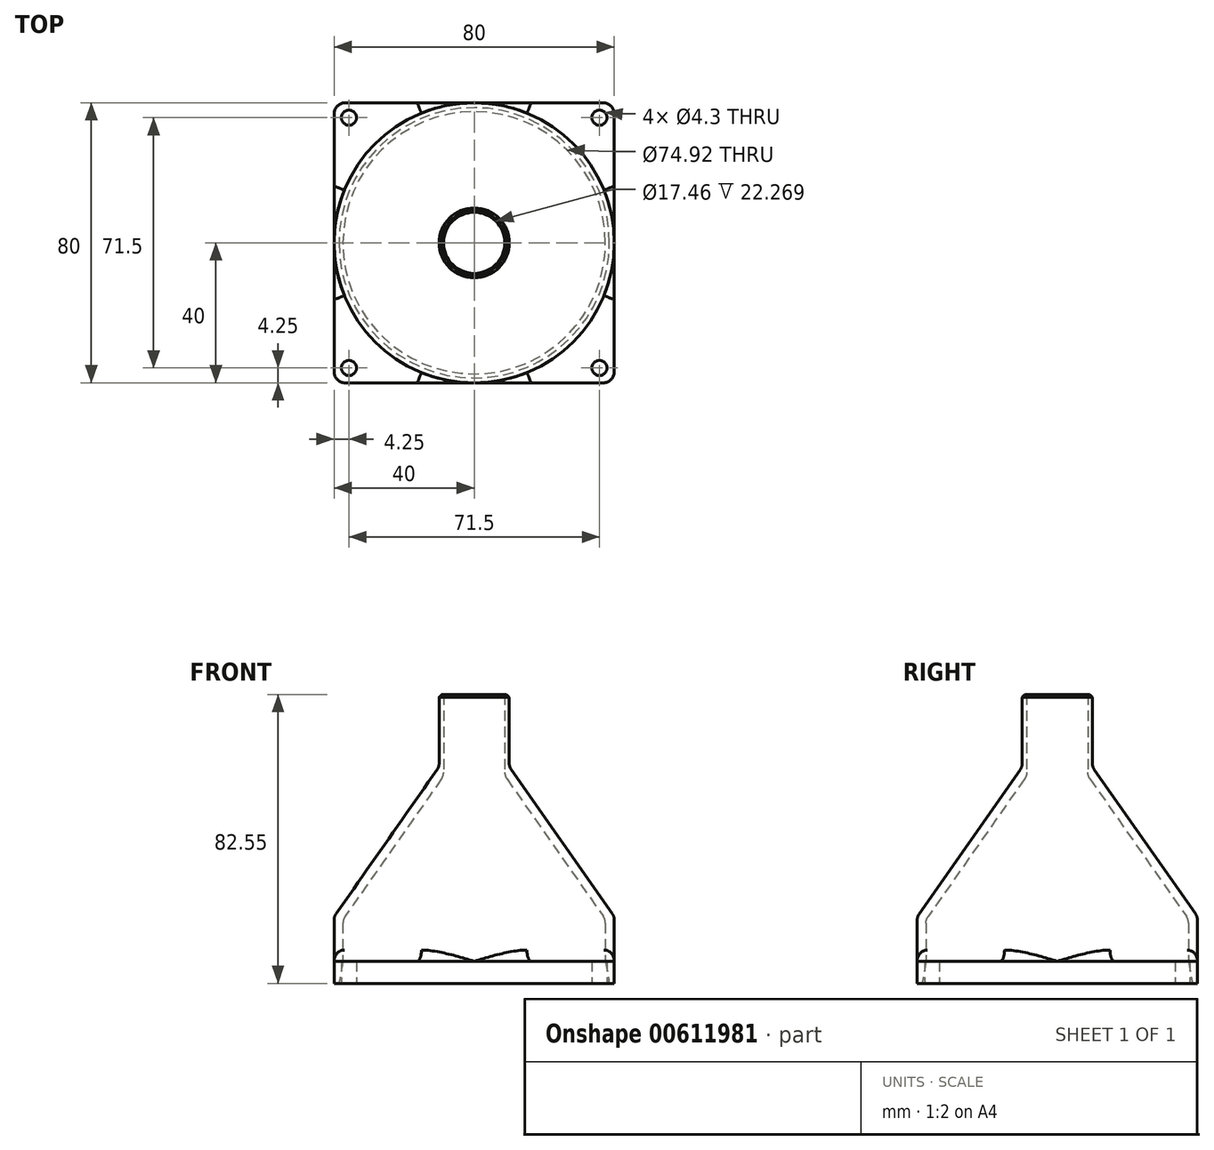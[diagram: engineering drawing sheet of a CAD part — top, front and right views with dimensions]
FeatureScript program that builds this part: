
annotation { "Feature Type Name" : "Feature", "Feature Type Description" : "" }
export const myFeature = defineFeature(function(context is Context, id is Id, definition is map)
    precondition{}
    {
        {
            var Q0;
            Q0=qCreatedBy(makeId("Top.planeOp"),FACE);
            var sketch = newSketch(context, id + "F0", { "sketchPlane" : qUnion([Q0])});
            skLineSegment(sketch, "E0.bottom", {"start": v(40, 40) * mm, "end": v(-40, 40) * mm});
            skLineSegment(sketch, "E0.top", {"start": v(40, -40) * mm, "end": v(-40, -40) * mm});
            skLineSegment(sketch, "E0.left", {"start": v(40, 40) * mm, "end": v(40, -40) * mm});
            skLineSegment(sketch, "E0.right", {"start": v(-40, 40) * mm, "end": v(-40, -40) * mm});
            skPoint(sketch, "E0.middle", {"position": v(0, 0) * mm});
            skSolve(sketch);
        }
        {
            var Q0;
            Q0 = qSketchRegion(id + "F0", true);
            extrude(context, id + "F1", {"entities" : qUnion([Q0]), "oppositeDirection" : true, "depth" : 6.35 * mm, "offsetDistance" : 25.4 * mm});
        }
        {
            var Q0;
            Q0=qCreatedBy(makeId("Front.planeOp"),FACE);
            var sketch = newSketch(context, id + "F2", { "sketchPlane" : qUnion([Q0])});
            skLineSegment(sketch, "E1", {"start": v(0, 0) * mm, "end": v(0, -6.35) * mm});
            skLineSegment(sketch, "E2", {"start": v(38.6, -6.35) * mm, "end": v(37.46, 0) * mm});
            skLineSegment(sketch, "E3", {"start": v(37.46, 0) * mm, "end": v(0, 0) * mm});
            skLineSegment(sketch, "E4", {"start": v(0, -6.35) * mm, "end": v(38.6, -6.35) * mm});
            skLineSegment(sketch, "E5", {"start": v(0, 0) * mm, "end": v(0, 10.75) * mm, "construction": true});
            skSolve(sketch);
        }
        {
            var Q0;
            Q0 = qSketchRegion(id + "F2", true);
            var Q1;
            Q1=sQuery(id+"F2.wireOp",EDGE,"E5");
            revolve(context, id + "F3", {"operationType" : NewBodyOperationType.REMOVE, "entities" : qUnion([Q0]), "axis" : qUnion([Q1]), "revolveType" : RevolveType.FULL, "oppositeDirection" : true});
        }
        {
            var Q0;
            Q0=qCreatedBy(makeId("Front.planeOp"),FACE);
            var sketch = newSketch(context, id + "F4", { "sketchPlane" : qUnion([Q0])});
            skLineSegment(sketch, "E6", {"start": v(37.46, 0) * mm, "end": v(37.46, 11.9) * mm});
            skLineSegment(sketch, "E7", {"start": v(37.46, 11.9) * mm, "end": v(8.73, 52.93) * mm});
            skLineSegment(sketch, "E8", {"start": v(8.73, 52.93) * mm, "end": v(8.73, 76.2) * mm});
            skLineSegment(sketch, "E9", {"start": v(8.73, 76.2) * mm, "end": v(10, 76.2) * mm});
            skLineSegment(sketch, "E10", {"start": v(10, 76.2) * mm, "end": v(10, 55.54) * mm});
            skLineSegment(sketch, "E11", {"start": v(10, 55.54) * mm, "end": v(40, 12.7) * mm});
            skLineSegment(sketch, "E12", {"start": v(40, 12.7) * mm, "end": v(40, 0) * mm});
            skLineSegment(sketch, "E13", {"start": v(40, 0) * mm, "end": v(37.46, 0) * mm});
            skLineSegment(sketch, "E14.0", {"start": v(-37.46, 0) * mm, "end": v(37.46, 0) * mm, "construction": true});
            skLineSegment(sketch, "E15", {"start": v(0, 0) * mm, "end": v(0, 76.2) * mm, "construction": true});
            skSolve(sketch);
        }
        {
            var Q0;
            Q0=makeQuery(id+"F4.imprint","IMPRINT",FACE,{"disambiguationData":[TD([[makeQuery(id+"F4.imprint","IMPRINT",EDGE,{"derivedFrom":sQuery(id+"F4.wireOp",EDGE,"E6")}),-1.0]])]});
            var Q1;
            Q1=sQuery(id+"F4.wireOp",EDGE,"E15");
            revolve(context, id + "F5", {"operationType" : NewBodyOperationType.ADD, "entities" : qUnion([Q0]), "axis" : qUnion([Q1]), "revolveType" : RevolveType.FULL});
        }
        {
            var Q0;
            Q0=makeQuery(id+"F1.opExtrude","CAP_FACE",FACE,{"disambiguationData":[OSD([sQuery(id+"F0.wireOp",EDGE,"E0.bottom"),sQuery(id+"F0.wireOp",EDGE,"E0.top"),sQuery(id+"F0.wireOp",EDGE,"E0.left"),sQuery(id+"F0.wireOp",EDGE,"E0.right")])],"isStart":false});
            var sketch = newSketch(context, id + "F6", { "sketchPlane" : qUnion([Q0])});
            skCircle(sketch, "E16", {"center": v(35.75, 35.75) * mm, "radius": 2.15 * mm});
            skCircle(sketch, "E17", {"center": v(-35.75, 35.75) * mm, "radius": 2.15 * mm});
            skCircle(sketch, "E18", {"center": v(-35.75, -35.75) * mm, "radius": 2.15 * mm});
            skCircle(sketch, "E19", {"center": v(35.75, -35.75) * mm, "radius": 2.15 * mm});
            skLineSegment(sketch, "E20", {"start": v(-35.75, -35.75) * mm, "end": v(35.75, 35.75) * mm, "construction": true});
            skSolve(sketch);
        }
        {
            var Q0;
            Q0 = qSketchRegion(id + "F6", true);
            extrude(context, id + "F7", {"entities" : qUnion([Q0]), "operationType" : NewBodyOperationType.REMOVE, "endBound" : BoundingType.UP_TO_NEXT, "oppositeDirection" : true, "depth" : 25.4 * mm, "offsetDistance" : 25.4 * mm});
        }
        {
            var Q0;
            Q0=makeQuery(id+"F5.opRevolve","SWEPT_EDGE",EDGE,{"disambiguationData":[OSD([sQuery(id+"F4.wireOp",EDGE,"E9"),sQuery(id+"F4.wireOp",EDGE,"E10")])]});
            chamfer(context, id + "F8", {"entities" : qUnion([Q0]), "width" : 0.76 * mm, "tangentPropagation" : true});
        }
        {
            var Q0;
            {var subQ0=sQuery(id+"F0.wireOp",EDGE,"E0.right");var subQ1=sQuery(id+"F0.wireOp",EDGE,"E0.top");var subQ2=sQuery(id+"F4.wireOp",EDGE,"E12");Q0=makeQuery(id+"F5.boolean.opBoolean","SPLIT",EDGE,{"disambiguationData":[TD([makeQuery(id+"F1.opExtrude","CAP_FACE",FACE,{"disambiguationData":[OSD([sQuery(id+"F0.wireOp",EDGE,"E0.bottom"),subQ1,sQuery(id+"F0.wireOp",EDGE,"E0.left"),subQ0])],"isStart":true}),makeQuery(id+"F1.opExtrude","SWEPT_FACE",FACE,{"disambiguationData":[OSD([subQ1])]}),makeQuery(id+"F1.opExtrude","SWEPT_FACE",FACE,{"disambiguationData":[OSD([subQ0])]}),makeQuery(id+"F5.opRevolve","SWEPT_FACE",FACE,{"disambiguationData":[OSD([subQ2])]})])],"derivedFrom":makeQuery(id+"F5.opRevolve","SWEPT_EDGE",EDGE,{"disambiguationData":[OSD([subQ2,sQuery(id+"F4.wireOp",EDGE,"E13")])]})});}
            var Q1;
            {var subQ0=sQuery(id+"F0.wireOp",EDGE,"E0.left");var subQ1=sQuery(id+"F0.wireOp",EDGE,"E0.top");var subQ2=sQuery(id+"F4.wireOp",EDGE,"E12");Q1=makeQuery(id+"F5.boolean.opBoolean","SPLIT",EDGE,{"disambiguationData":[TD([makeQuery(id+"F1.opExtrude","CAP_FACE",FACE,{"disambiguationData":[OSD([sQuery(id+"F0.wireOp",EDGE,"E0.bottom"),subQ1,subQ0,sQuery(id+"F0.wireOp",EDGE,"E0.right")])],"isStart":true}),makeQuery(id+"F1.opExtrude","SWEPT_FACE",FACE,{"disambiguationData":[OSD([subQ1])]}),makeQuery(id+"F1.opExtrude","SWEPT_FACE",FACE,{"disambiguationData":[OSD([subQ0])]}),makeQuery(id+"F5.opRevolve","SWEPT_FACE",FACE,{"disambiguationData":[OSD([subQ2])]})])],"derivedFrom":makeQuery(id+"F5.opRevolve","SWEPT_EDGE",EDGE,{"disambiguationData":[OSD([subQ2,sQuery(id+"F4.wireOp",EDGE,"E13")])]})});}
            var Q2;
            {var subQ0=sQuery(id+"F0.wireOp",EDGE,"E0.bottom");var subQ1=sQuery(id+"F0.wireOp",EDGE,"E0.left");var subQ2=sQuery(id+"F4.wireOp",EDGE,"E12");Q2=makeQuery(id+"F5.boolean.opBoolean","SPLIT",EDGE,{"disambiguationData":[TD([makeQuery(id+"F1.opExtrude","SWEPT_FACE",FACE,{"disambiguationData":[OSD([subQ0])]}),makeQuery(id+"F1.opExtrude","CAP_FACE",FACE,{"disambiguationData":[OSD([subQ0,sQuery(id+"F0.wireOp",EDGE,"E0.top"),subQ1,sQuery(id+"F0.wireOp",EDGE,"E0.right")])],"isStart":true}),makeQuery(id+"F1.opExtrude","SWEPT_FACE",FACE,{"disambiguationData":[OSD([subQ1])]}),makeQuery(id+"F5.opRevolve","SWEPT_FACE",FACE,{"disambiguationData":[OSD([subQ2])]})])],"derivedFrom":makeQuery(id+"F5.opRevolve","SWEPT_EDGE",EDGE,{"disambiguationData":[OSD([subQ2,sQuery(id+"F4.wireOp",EDGE,"E13")])]})});}
            var Q3;
            {var subQ0=sQuery(id+"F0.wireOp",EDGE,"E0.bottom");var subQ1=sQuery(id+"F0.wireOp",EDGE,"E0.right");var subQ2=sQuery(id+"F4.wireOp",EDGE,"E12");Q3=makeQuery(id+"F5.boolean.opBoolean","SPLIT",EDGE,{"disambiguationData":[TD([makeQuery(id+"F1.opExtrude","SWEPT_FACE",FACE,{"disambiguationData":[OSD([subQ0])]}),makeQuery(id+"F1.opExtrude","CAP_FACE",FACE,{"disambiguationData":[OSD([subQ0,sQuery(id+"F0.wireOp",EDGE,"E0.top"),sQuery(id+"F0.wireOp",EDGE,"E0.left"),subQ1])],"isStart":true}),makeQuery(id+"F1.opExtrude","SWEPT_FACE",FACE,{"disambiguationData":[OSD([subQ1])]}),makeQuery(id+"F5.opRevolve","SWEPT_FACE",FACE,{"disambiguationData":[OSD([subQ2])]})])],"derivedFrom":makeQuery(id+"F5.opRevolve","SWEPT_EDGE",EDGE,{"disambiguationData":[OSD([subQ2,sQuery(id+"F4.wireOp",EDGE,"E13")])]})});}
            var Q4;
            Q4=makeQuery(id+"F5.opRevolve","SWEPT_EDGE",EDGE,{"disambiguationData":[OSD([sQuery(id+"F4.wireOp",EDGE,"E11"),sQuery(id+"F4.wireOp",EDGE,"E12")])]});
            var Q5;
            Q5=makeQuery(id+"F5.opRevolve","SWEPT_EDGE",EDGE,{"disambiguationData":[OSD([sQuery(id+"F4.wireOp",EDGE,"E6"),sQuery(id+"F4.wireOp",EDGE,"E7")])]});
            var Q6;
            Q6=makeQuery(id+"F5.opRevolve","SWEPT_EDGE",EDGE,{"disambiguationData":[OSD([sQuery(id+"F4.wireOp",EDGE,"E10"),sQuery(id+"F4.wireOp",EDGE,"E11")])]});
            var Q7;
            Q7=makeQuery(id+"F5.opRevolve","SWEPT_EDGE",EDGE,{"disambiguationData":[OSD([sQuery(id+"F4.wireOp",EDGE,"E7"),sQuery(id+"F4.wireOp",EDGE,"E8")])]});
            var Q8;
            Q8=makeQuery(id+"F1.opExtrude","SWEPT_EDGE",EDGE,{"disambiguationData":[OSD([sQuery(id+"F0.wireOp",EDGE,"E0.bottom"),sQuery(id+"F0.wireOp",EDGE,"E0.left")])]});
            var Q9;
            Q9=makeQuery(id+"F1.opExtrude","SWEPT_EDGE",EDGE,{"disambiguationData":[OSD([sQuery(id+"F0.wireOp",EDGE,"E0.bottom"),sQuery(id+"F0.wireOp",EDGE,"E0.right")])]});
            var Q10;
            Q10=makeQuery(id+"F1.opExtrude","SWEPT_EDGE",EDGE,{"disambiguationData":[OSD([sQuery(id+"F0.wireOp",EDGE,"E0.top"),sQuery(id+"F0.wireOp",EDGE,"E0.right")])]});
            var Q11;
            Q11=makeQuery(id+"F1.opExtrude","SWEPT_EDGE",EDGE,{"disambiguationData":[OSD([sQuery(id+"F0.wireOp",EDGE,"E0.top"),sQuery(id+"F0.wireOp",EDGE,"E0.left")])]});
            fillet(context, id + "F9", {"entities" : qUnion([Q0, Q1, Q2, Q3, Q4, Q5, Q6, Q7, Q8, Q9, Q10, Q11]), "radius" : 3.17 * mm, "tangentPropagation" : true, "allowEdgeOverflow" : false});
        }
    });
